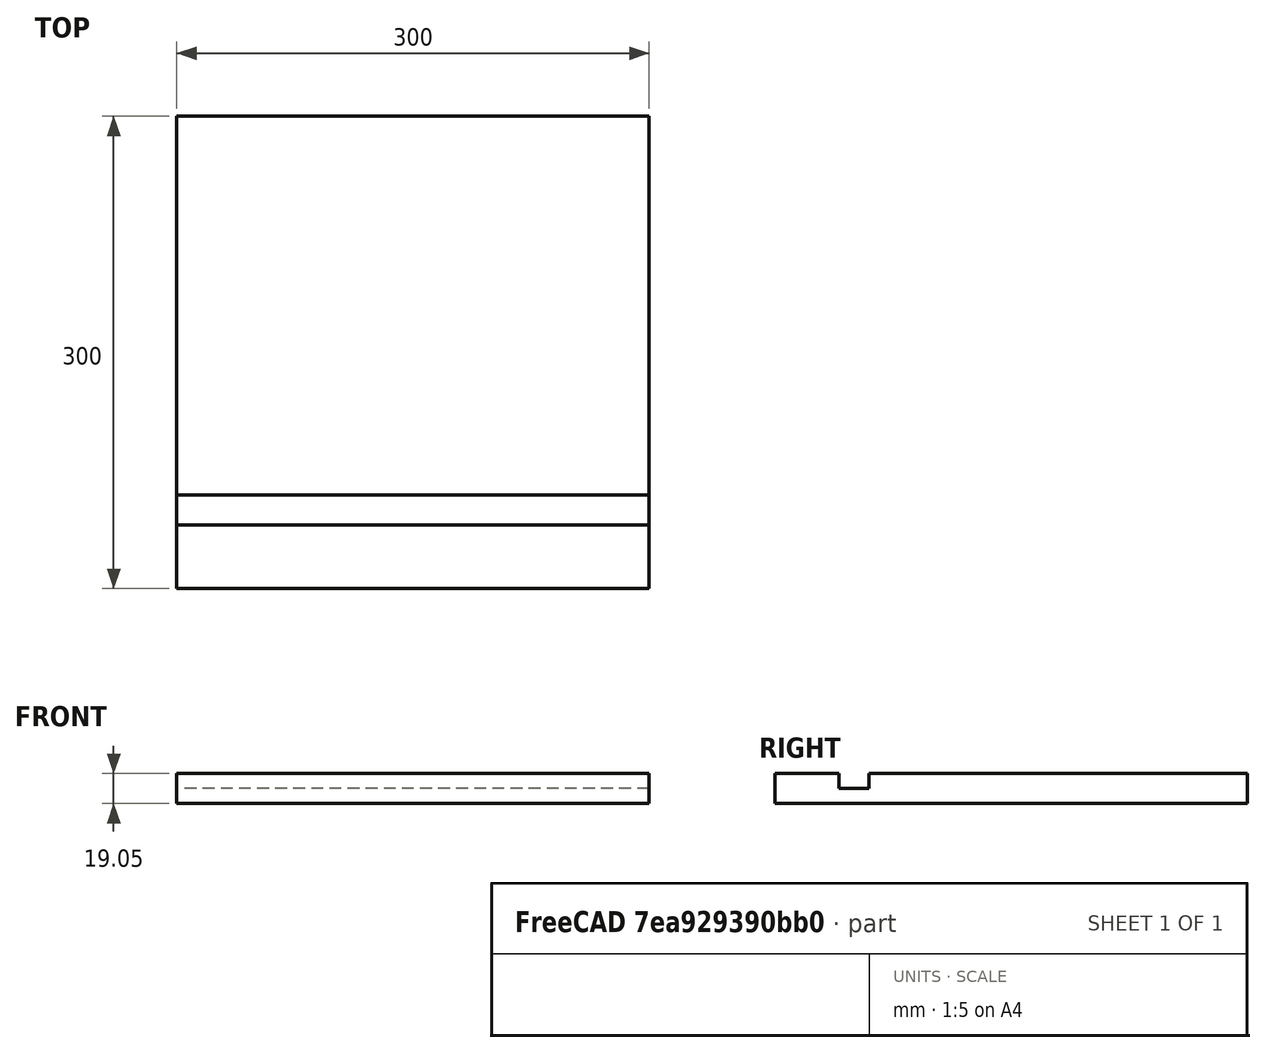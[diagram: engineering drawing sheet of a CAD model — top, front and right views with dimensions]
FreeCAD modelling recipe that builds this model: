
FCSTD DOCUMENT  (FreeCAD 0.19R24291 (Git))
Label: base
License: All rights reserved
LicenseURL: http://en.wikipedia.org/wiki/All_rights_reserved
objects: TechDraw::DrawViewDimension×3, Sketcher::SketchObject×2, PartDesign::Pad×1, PartDesign::Pocket×1, PartDesign::Body×1, TechDraw::DrawSVGTemplate×1, TechDraw::DrawViewPart×1, TechDraw::DrawPage×1
note: 7 computed .brp shape members not serialized (recipe doc carries the construction recipe); baked Part::Feature solids carry a one-line shape summary decoded from their .brp

FEATURE [Sketcher::SketchObject] Sketch
  FullyConstrained = false
  MapMode = 5
  Support = -> [XY_Plane]
  expr: Constraints[17] = 3.5 * 25.4
  expr: Constraints[40] = 3.5 * 25.4
  sketch-geometry (20):
    g0: LineSegment StartX=0 StartY=0 StartZ=0 EndX=300 EndY=0 EndZ=0
    g1: LineSegment StartX=300 StartY=0 StartZ=0 EndX=300 EndY=300 EndZ=0
    g2: LineSegment StartX=300 StartY=300 StartZ=0 EndX=0 EndY=300 EndZ=0
    g3: LineSegment StartX=0 StartY=300 StartZ=0 EndX=0 EndY=0 EndZ=0
    g4: LineSegment StartX=100 StartY=-142.898 StartZ=0 EndX=188.9 EndY=-142.898 EndZ=0
    g5: LineSegment StartX=188.9 StartY=-142.898 StartZ=0 EndX=188.9 EndY=188.9 EndZ=0
    g6: LineSegment StartX=188.9 StartY=188.9 StartZ=0 EndX=100 EndY=188.9 EndZ=0
    g7: LineSegment StartX=100 StartY=188.9 StartZ=0 EndX=100 EndY=-142.898 EndZ=0
    g8: LineSegment StartX=0 StartY=0 StartZ=0 EndX=100 EndY=0 EndZ=0
    g9: LineSegment StartX=100 StartY=0 StartZ=0 EndX=100 EndY=100 EndZ=0
    g10: LineSegment StartX=100 StartY=100 StartZ=0 EndX=0 EndY=100 EndZ=0
    g11: LineSegment StartX=0 StartY=100 StartZ=0 EndX=0 EndY=0 EndZ=0
    g12: LineSegment StartX=-106.303 StartY=188.9 StartZ=0 EndX=100 EndY=188.9 EndZ=0
    g13: LineSegment StartX=100 StartY=188.9 StartZ=0 EndX=100 EndY=100 EndZ=0
    g14: LineSegment StartX=100 StartY=100 StartZ=0 EndX=-106.303 EndY=100 EndZ=0
    g15: LineSegment StartX=-106.303 StartY=100 StartZ=0 EndX=-106.303 EndY=188.9 EndZ=0
    g16: LineSegment StartX=203.967 StartY=100 StartZ=0 EndX=253.967 EndY=100 EndZ=0
    g17: LineSegment StartX=253.967 StartY=100 StartZ=0 EndX=253.967 EndY=0 EndZ=0
    g18: LineSegment StartX=253.967 StartY=0 StartZ=0 EndX=203.967 EndY=0 EndZ=0
    g19: LineSegment StartX=203.967 StartY=0 StartZ=0 EndX=203.967 EndY=100 EndZ=0
  constraints (54):
    c: Coincident(g0,g1)
    c: Coincident(g1,g2)
    c: Coincident(g2,g3)
    c: Coincident(g3,g0)
    c: Horizontal(g0)
    c: Horizontal(g2)
    c: Vertical(g1)
    c: Vertical(g3)
    c: Coincident(g0,g-1)
    c: Coincident(g4,g5)
    c: Coincident(g5,g6)
    c: Coincident(g6,g7)
    c: Coincident(g7,g4)
    c: Horizontal(g4)
    c: Horizontal(g6)
    c: Vertical(g5)
    c: Vertical(g7)
    c: DistanceX(g4,g4) = 88.9
    c: Coincident(g8,g9)
    c: Coincident(g9,g10)
    c: Coincident(g10,g11)
    c: Coincident(g11,g8)
    c: Horizontal(g8)
    c: Horizontal(g10)
    c: Vertical(g9)
    c: Vertical(g11)
    c: Coincident(g8,g0)
    c: DistanceX(g10,g10) = 100
    c: DistanceY(g9,g9) = 100
    c: PointOnObject(g8,g7)
    c: DistanceX(g0,g0) = 300
    c: DistanceY(g3,g3) = 300
    c: Coincident(g12,g13)
    c: Coincident(g13,g14)
    c: Coincident(g14,g15)
    c: Coincident(g15,g12)
    c: Horizontal(g12)
    c: Horizontal(g14)
    c: Vertical(g13)
    c: Vertical(g15)
    c: DistanceY(g15,g15) = 88.9
    c: PointOnObject(g10,g14)
    c: Coincident(g12,g6)
    c: Coincident(g16,g17)
    c: Coincident(g17,g18)
    c: Coincident(g18,g19)
    c: Coincident(g19,g16)
    c: Horizontal(g16)
    c: Horizontal(g18)
    c: Vertical(g17)
    c: Vertical(g19)
    c: DistanceY(g19,g19) = 100
    c: DistanceX(g18,g18) = 50
    c: PointOnObject(g18,g0)
FEATURE [PartDesign::Pad] Pad
  Direction = (1,1,1)
  Length = 19.05
  Length2 = 100
  Profile = -> Sketch
  Type = 0
  expr: Length = 3 / 4 * 25.4
FEATURE [Sketcher::SketchObject] Sketch001
  ExternalGeometry = -> [Pad]
  FullyConstrained = false
  MapMode = 5
  Placement = pos=(300,0,0) rot=(0.57735,0.57735,0.57735;2.0944rad)
  Support = -> [Pad]
  expr: Constraints[9] = 3 / 4 * 25.4
  expr: Constraints[8] = 3 / 8 * 25.4
  sketch-geometry (5):
    g0: LineSegment StartX=40.475 StartY=19.05 StartZ=0 EndX=59.525 EndY=19.05 EndZ=0
    g1: LineSegment StartX=59.525 StartY=19.05 StartZ=0 EndX=59.525 EndY=9.525 EndZ=0
    g2: LineSegment StartX=59.525 StartY=9.525 StartZ=0 EndX=40.475 EndY=9.525 EndZ=0
    g3: LineSegment StartX=40.475 StartY=9.525 StartZ=0 EndX=40.475 EndY=19.05 EndZ=0
    g4: LineSegment StartX=50 StartY=19.05 StartZ=0 EndX=50 EndY=-17.5268 EndZ=0
  constraints (14):
    c: Coincident(g0,g1)
    c: Coincident(g1,g2)
    c: Coincident(g2,g3)
    c: Coincident(g3,g0)
    c: Horizontal(g0)
    c: Horizontal(g2)
    c: Vertical(g1)
    c: Vertical(g3)
    c: DistanceY(g1,g1) = 9.525
    c: DistanceX(g2,g2) = 19.05
    c: Vertical(g4)
    c: Symmetric(g0,g0,g4)
    c: DistanceX(g-3,g4) = 50
    c: PointOnObject(g0,g-3)
FEATURE [PartDesign::Pocket] Pocket
  BaseFeature = -> Pad
  Length = 5
  Length2 = 100
  Profile = -> Sketch001
  Type = 1
FEATURE [PartDesign::Body] Body
  Group = -> [Sketch,Pad,Sketch001,Pocket]
  Origin = -> Origin
  Tip = -> Pocket
FEATURE [TechDraw::DrawSVGTemplate] Template
  EditableTexts = APPROVER_NAME=APPROVER NAME; AUTHOR_NAME=AUTHOR NAME; DATE=YYYY-MM-DD; DN=DN; DOCUMENT_TYPE=Mechanical assembly drawing; OWNER_NAME=OWNER NAME; PM=PM; PN=PN; REVISION=REV A; RIGHTS=(R) DO NOT DUPLICATE THIS DRAWING TO THIRD PARTIES WITHOUT OWNER'S PERMISSION !; SCALE=M x:x; SHEET=99 of 99; SIZE=A4; TITLELINE-1=FreeCAD; TOLERANCE=+/- ?
  Height = 210
  Orientation = 1
  Width = 297
FEATURE [TechDraw::DrawViewPart] View
  CoarseView = false
  Direction = (0,0,1)
  Focus = 100
  HardHidden = false
  IsoCount = 0
  IsoHidden = false
  IsoVisible = false
  LockPosition = false
  Perspective = false
  Rotation = 0
  Scale = 0.3
  ScaleType = 0
  SeamHidden = false
  SeamVisible = true
  SmoothHidden = false
  SmoothVisible = true
  Source = -> [Body]
  X = 148.5
  XDirection = (1,0,0)
  Y = 105
FEATURE [TechDraw::DrawViewDimension] Dimension
  Arbitrary = false
  ArbitraryTolerances = false
  EqualTolerance = true
  FormatSpec = %.2f
  FormatSpecOverTolerance = %+.2f
  FormatSpecUnderTolerance = %+.2f
  Inverted = false
  LockPosition = false
  MeasureType = 1
  OverTolerance = 0
  References2D = -> [View]
  Rotation = 0
  ScaleType = 0
  TheoreticalExact = false
  Type = 1
  UnderTolerance = 0
  X = 0
  Y = 45
FEATURE [TechDraw::DrawViewDimension] Dimension002
  Arbitrary = false
  ArbitraryTolerances = false
  EqualTolerance = true
  FormatSpec = %.2f
  FormatSpecOverTolerance = %+.2f
  FormatSpecUnderTolerance = %+.2f
  Inverted = false
  LockPosition = false
  MeasureType = 1
  OverTolerance = 0
  References2D = -> [View]
  Rotation = 0
  ScaleType = 0
  TheoreticalExact = false
  Type = 2
  UnderTolerance = 0
  X = 78.4884
  Y = -0.382239
FEATURE [TechDraw::DrawViewDimension] Dimension003
  Arbitrary = false
  ArbitraryTolerances = false
  EqualTolerance = true
  FormatSpec = %.2f
  FormatSpecOverTolerance = %+.2f
  FormatSpecUnderTolerance = %+.2f
  Inverted = false
  LockPosition = false
  MeasureType = 1
  OverTolerance = 0
  References2D = -> [View]
  Rotation = 0
  ScaleType = 0
  TheoreticalExact = false
  Type = 2
  UnderTolerance = 0
  X = -75.6977
  Y = -1.22093
FEATURE [TechDraw::DrawPage] Page
  KeepUpdated = true
  NextBalloonIndex = 1
  ProjectionType = 0
  Template = -> Template
  Views = -> [View,Dimension,Dimension002,Dimension003]
